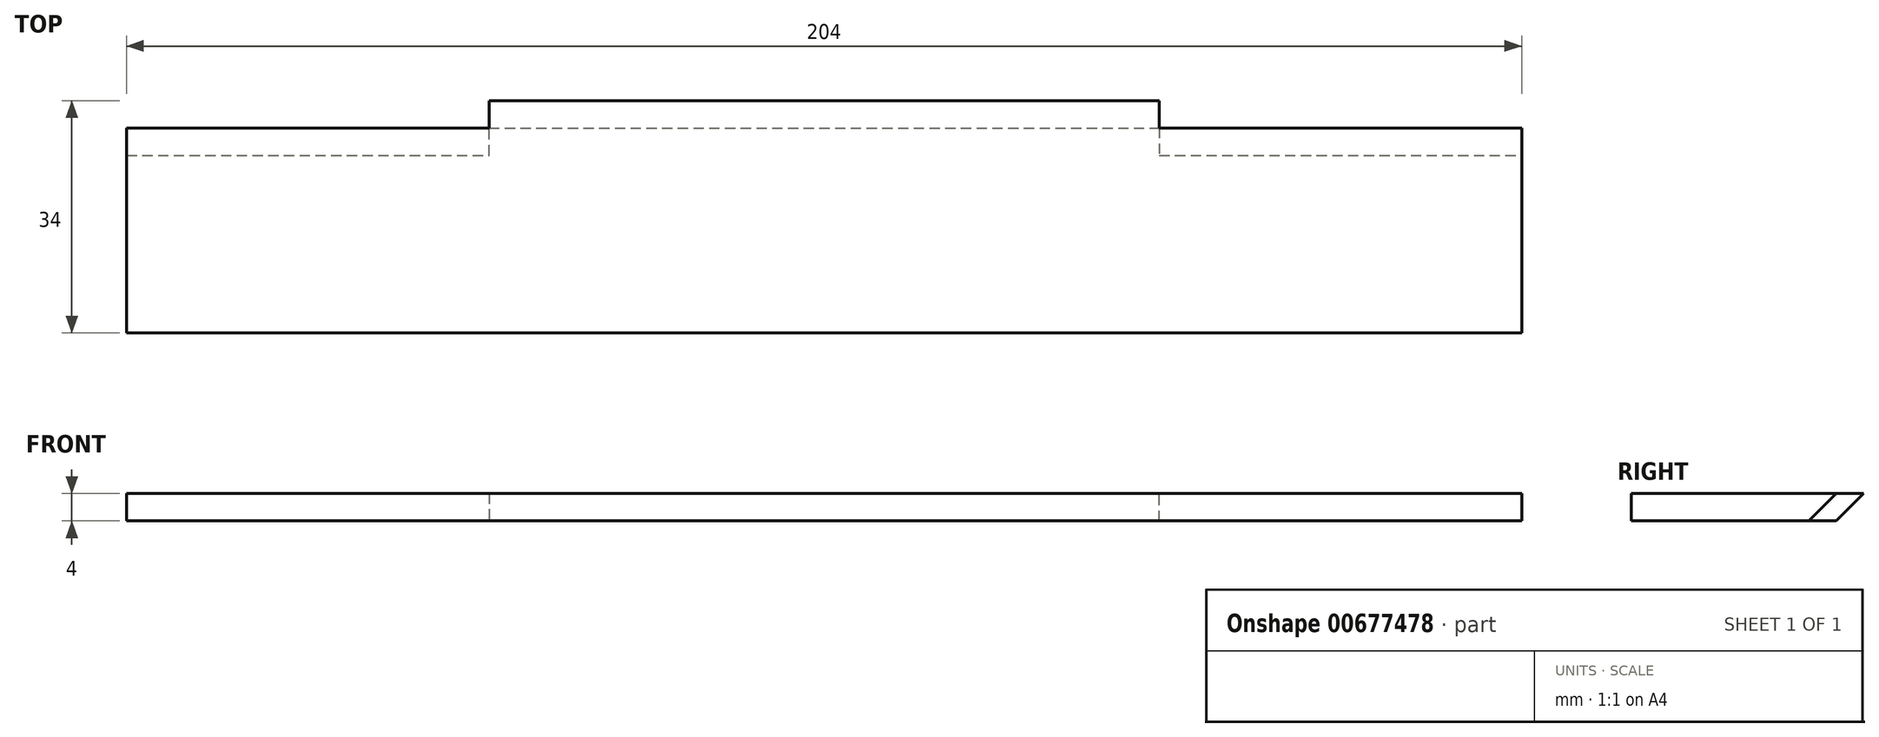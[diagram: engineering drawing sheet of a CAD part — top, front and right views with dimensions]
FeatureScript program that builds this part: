
annotation { "Feature Type Name" : "Feature", "Feature Type Description" : "" }
export const myFeature = defineFeature(function(context is Context, id is Id, definition is map)
    precondition{}
    {
        {
            var Q0;
            Q0=qCreatedBy(makeId("Top.planeOp"),FACE);
            var sketch = newSketch(context, id + "F0", { "sketchPlane" : qUnion([Q0])});
            skLineSegment(sketch, "E0", {"start": v(0, 0) * mm, "end": v(102, 0) * mm});
            skLineSegment(sketch, "E1", {"start": v(102, 0) * mm, "end": v(-102, 0) * mm});
            skLineSegment(sketch, "E2", {"start": v(-102, 0) * mm, "end": v(-102, 30) * mm});
            skLineSegment(sketch, "E3", {"start": v(102, 30) * mm, "end": v(102, 0) * mm});
            skLineSegment(sketch, "E4", {"start": v(-102, 30) * mm, "end": v(-49, 30) * mm});
            skLineSegment(sketch, "E5", {"start": v(-49, 30) * mm, "end": v(-49, 34) * mm});
            skLineSegment(sketch, "E6", {"start": v(-49, 34) * mm, "end": v(49, 34) * mm});
            skLineSegment(sketch, "E7", {"start": v(49, 34) * mm, "end": v(49, 30) * mm});
            skLineSegment(sketch, "E8", {"start": v(49, 30) * mm, "end": v(102, 30) * mm});
            skSolve(sketch);
        }
        {
            var Q0;
            {var subQ1=sQuery(id+"F0.wireOp",EDGE,"E2");Q0=makeQuery(id+"F0.imprint","IMPRINT",FACE,{"disambiguationData":[TD([[makeQuery(id+"F0.imprint","IMPRINT",EDGE,{"derivedFrom":subQ1}),-1.0]])]});}
            extrude(context, id + "F1", {"entities" : qUnion([Q0]), "depth" : 4 * mm, "offsetDistance" : 25 * mm});
        }
        {
            var Q0;
            Q0=makeQuery(id+"F1.opExtrude","CAP_EDGE",EDGE,{"disambiguationData":[OSD([sQuery(id+"F0.wireOp",EDGE,"E8")])],"isStart":true});
            chamfer(context, id + "F2", {"entities" : qUnion([Q0]), "width" : 4 * mm, "tangentPropagation" : true});
        }
        {
            var Q0;
            Q0=makeQuery(id+"F1.opExtrude","CAP_EDGE",EDGE,{"disambiguationData":[OSD([sQuery(id+"F0.wireOp",EDGE,"E6")])],"isStart":true});
            chamfer(context, id + "F3", {"entities" : qUnion([Q0]), "width" : 4 * mm, "tangentPropagation" : true});
        }
        {
            var Q0;
            Q0=makeQuery(id+"F1.opExtrude","CAP_EDGE",EDGE,{"disambiguationData":[OSD([sQuery(id+"F0.wireOp",EDGE,"E4")])],"isStart":true});
            chamfer(context, id + "F4", {"entities" : qUnion([Q0]), "width" : 4 * mm, "tangentPropagation" : true});
        }
    });
